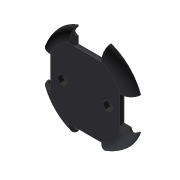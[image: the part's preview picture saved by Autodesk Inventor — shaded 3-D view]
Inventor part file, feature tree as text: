
AUTODESK INVENTOR PART (.ipt)
format: ipt  version: 2017 (Build 210142000, 142)  size: 185,856 bytes
history: native  units: mm
features: sketch x5, extrude x3, revolve x1, fillet x1, pattern_circular x1, hole x1, projected_geometry x1
ambient origin geometry x8: Origin, YZ Plane, XZ Plane, XY Plane, X Axis, Y Axis, Z Axis, Center Point
bodies: Solid1 (feature_tree)
feature tree (13):
  extrude  "Extrusion1"  Depth=6.0mm TaperAngle=0.0deg
  revolve  "Revolution1"  [1 undecoded]
  extrude  "Extrusion2"  Depth=5.0mm
  fillet  "Fillet1"  Radius=5.0mm
  pattern_circular  "Circular Pattern1"  [2 undecoded]
  hole  "Hole1"  [1 undecoded]
  extrude  "Extrusion3"  Depth=3.0mm
  sketch  "Sketch1"  dims[d0=60.0mm d1=6.0mm d2=0.0mm]
  sketch  "Sketch2"  dims[d3=20.0mm d4=25.0mm]
  sketch  "Sketch3"  dims[d5=14.0mm d6=5.0mm d7=5.0mm]
  projected_geometry  "Projected Loop1"
  sketch  "Sketch4"  dims[d8=90.0deg]
  sketch  "Sketch5"  dims[d9=6.0mm d10=0.0mm d11=6.0mm d12=40.0mm d13=360.0deg d15=14.0mm d16=14.0mm d17=4.0mm d18=6.0mm d19=4.0mm d20=2.0mm d21=90.0deg d22=8.0mm d23=20.594885mm d24=5.5mm d25=5.5mm d26=3.0mm d27=0.0mm]
note: 4 required parameter values undecoded (feature->parameter linkage not recoverable at this tier; creation-order binding heuristic only, values carry confidence <= 0.55)